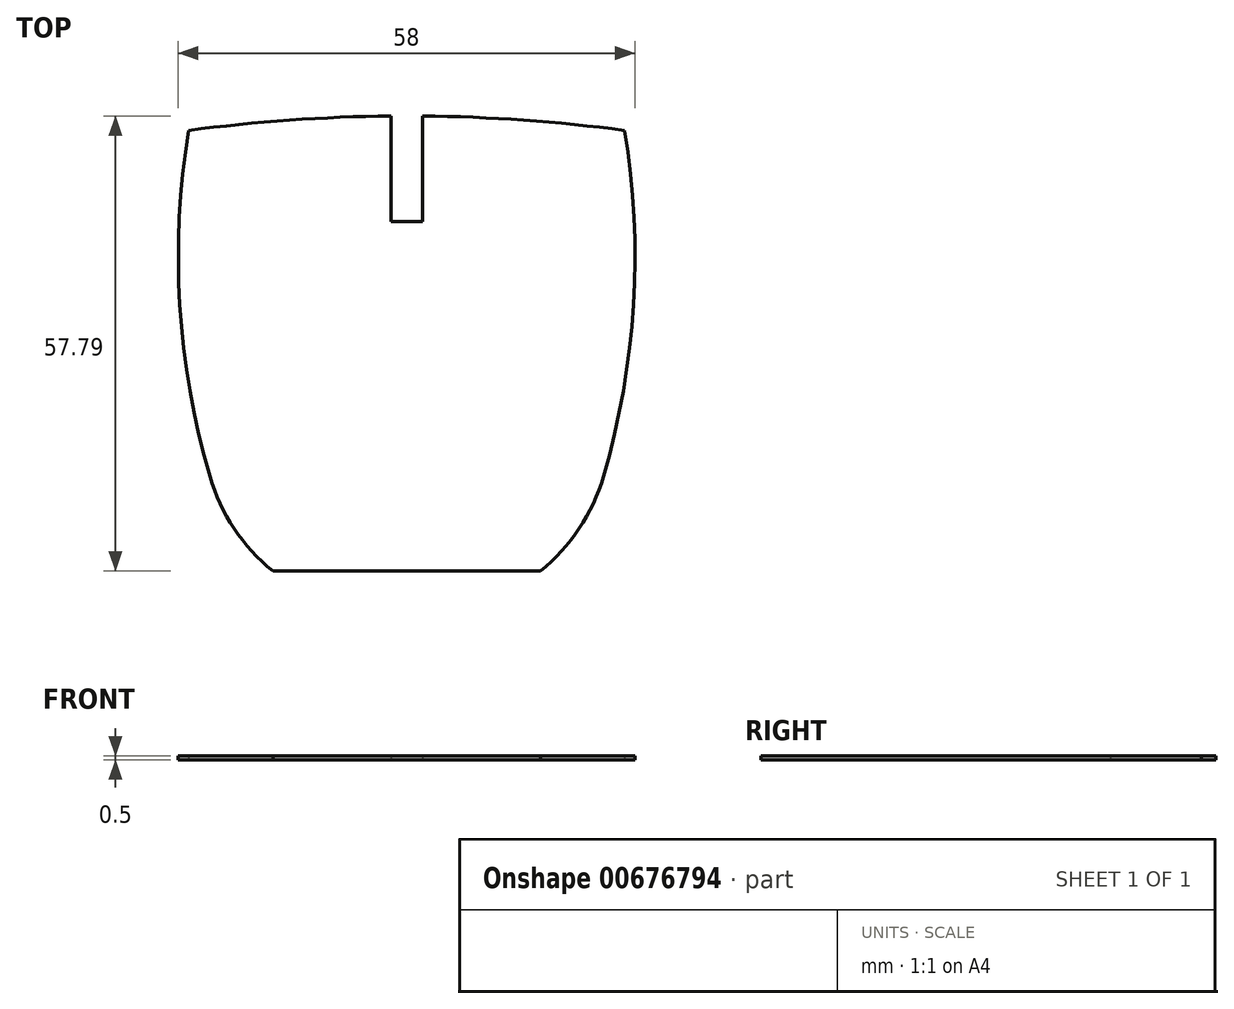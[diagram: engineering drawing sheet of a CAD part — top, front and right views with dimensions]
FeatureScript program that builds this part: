
annotation { "Feature Type Name" : "Feature", "Feature Type Description" : "" }
export const myFeature = defineFeature(function(context is Context, id is Id, definition is map)
    precondition{}
    {
        {
            var Q0;
            Q0=qCreatedBy(makeId("Top.planeOp"),FACE);
            var sketch = newSketch(context, id + "F0", { "sketchPlane" : qUnion([Q0])});
            skLineSegment(sketch, "E0", {"start": v(-25, 56.3) * mm, "end": v(-25, 12) * mm, "construction": true});
            skLineSegment(sketch, "E1", {"start": v(-25, 0) * mm, "end": v(-17, 0) * mm, "construction": true});
            skLineSegment(sketch, "E2", {"start": v(25, 0) * mm, "end": v(25, 12) * mm, "construction": true});
            skArc(sketch, "E3", {"start": v(-25, 56.3) * mm, "mid": v(-13.52, 57.36) * mm, "end": v(-2, 57.8) * mm});
            skPoint(sketch, "E4", {"position": v(0, 57.8) * mm});
            skLineSegment(sketch, "E5", {"start": v(-2, 57.8) * mm, "end": v(-2, 44.4) * mm});
            skLineSegment(sketch, "E6", {"start": v(-2, 44.4) * mm, "end": v(2, 44.4) * mm});
            skLineSegment(sketch, "E7", {"start": v(2, 44.4) * mm, "end": v(2, 57.8) * mm});
            skArc(sketch, "E8", {"start": v(-2, 57.8) * mm, "mid": v(0, 57.8) * mm, "end": v(2, 57.8) * mm, "construction": true});
            skArc(sketch, "E9", {"start": v(2, 57.8) * mm, "mid": v(13.52, 57.36) * mm, "end": v(25, 56.3) * mm});
            skPoint(sketch, "E10", {"position": v(-17, 0) * mm});
            skPoint(sketch, "E11", {"position": v(17, 0) * mm});
            skPoint(sketch, "E12", {"position": v(25, 12) * mm});
            skPoint(sketch, "E13", {"position": v(-25, 12) * mm});
            skLineSegment(sketch, "E14", {"start": v(25, 12) * mm, "end": v(25, 56.3) * mm, "construction": true});
            skLineSegment(sketch, "E15", {"start": v(17, 0) * mm, "end": v(25, 0) * mm, "construction": true});
            skLineSegment(sketch, "E16", {"start": v(-17, 0) * mm, "end": v(17, 0) * mm});
            skLineSegment(sketch, "E17", {"start": v(-25, 12) * mm, "end": v(-25, 0) * mm, "construction": true});
            skArc(sketch, "E18", {"start": v(17, 0) * mm, "mid": v(21.92, 5.39) * mm, "end": v(25, 12) * mm});
            skArc(sketch, "E19", {"start": v(-25, 12) * mm, "mid": v(-21.92, 5.39) * mm, "end": v(-17, 0) * mm});
            skArc(sketch, "E20", {"start": v(-25, 56.3) * mm, "mid": v(-26.35, 56.13) * mm, "end": v(-27.7, 55.96) * mm});
            skArc(sketch, "E21", {"start": v(25, 56.3) * mm, "mid": v(26.35, 56.13) * mm, "end": v(27.7, 55.96) * mm});
            skArc(sketch, "E22", {"start": v(-27.7, 55.96) * mm, "mid": v(-28.81, 33.83) * mm, "end": v(-25, 12) * mm});
            skPoint(sketch, "E23", {"position": v(-29, 39.93) * mm});
            skLineSegment(sketch, "E24", {"start": v(-29, 39.93) * mm, "end": v(-29, 46.45) * mm, "construction": true});
            skArc(sketch, "E25", {"start": v(25, 12) * mm, "mid": v(28.81, 33.83) * mm, "end": v(27.7, 55.96) * mm});
            skPoint(sketch, "E26", {"position": v(29, 39.93) * mm});
            skLineSegment(sketch, "E27", {"start": v(29, 39.93) * mm, "end": v(29, 59.06) * mm, "construction": true});
            skSolve(sketch);
        }
        {
            var Q0;
            Q0 = qSketchRegion(id + "F0", true);
            extrude(context, id + "F1", {"entities" : qUnion([Q0]), "depth" : 0.5 * mm, "offsetDistance" : 25 * mm});
        }
    });
